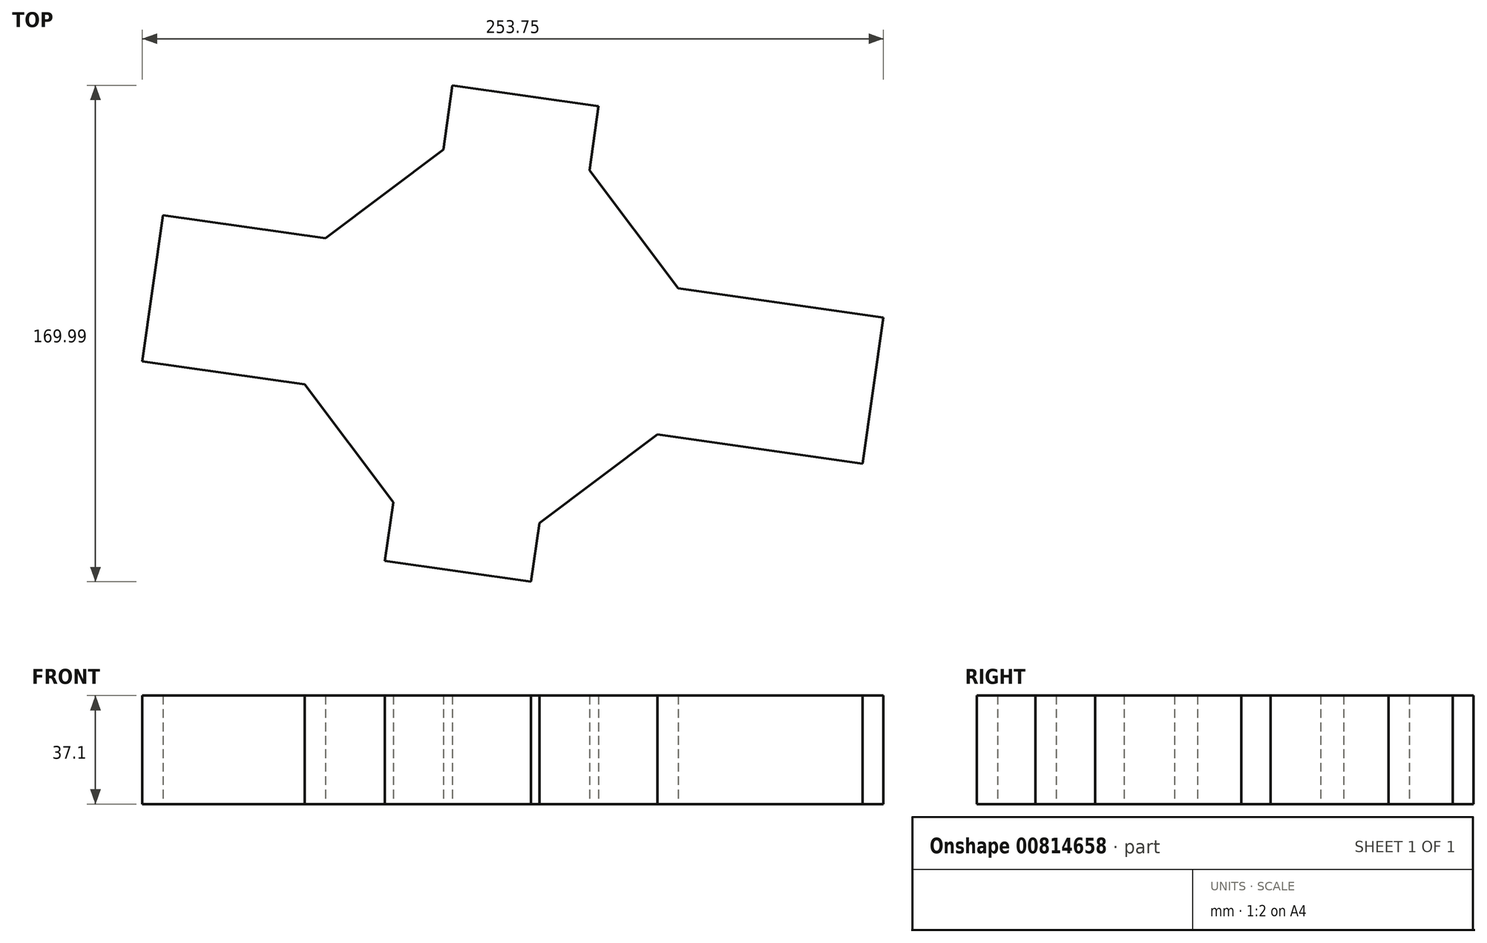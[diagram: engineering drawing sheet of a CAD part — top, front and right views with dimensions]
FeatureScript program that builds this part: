
annotation { "Feature Type Name" : "Feature", "Feature Type Description" : "" }
export const myFeature = defineFeature(function(context is Context, id is Id, definition is map)
    precondition{}
    {
        {
            var Q0;
            Q0=qCreatedBy(makeId("Top.planeOp"),FACE);
            var sketch = newSketch(context, id + "F0", { "sketchPlane" : qUnion([Q0])});
            skCircle(sketch, "E0.cCircle", {"center": v(0, 0) * mm, "radius": 61 * mm, "construction": true});
            skLineSegment(sketch, "E0.0", {"start": v(-63.96, -16.44) * mm, "end": v(-56.85, 33.6) * mm});
            skLineSegment(sketch, "E0.1", {"start": v(-56.85, 33.6) * mm, "end": v(-16.44, 63.96) * mm});
            skLineSegment(sketch, "E0.2", {"start": v(-16.44, 63.96) * mm, "end": v(33.6, 56.85) * mm});
            skLineSegment(sketch, "E0.3", {"start": v(33.6, 56.85) * mm, "end": v(63.96, 16.44) * mm});
            skLineSegment(sketch, "E0.4", {"start": v(63.96, 16.44) * mm, "end": v(56.85, -33.6) * mm});
            skLineSegment(sketch, "E0.5", {"start": v(56.85, -33.6) * mm, "end": v(16.44, -63.96) * mm});
            skLineSegment(sketch, "E0.6", {"start": v(16.44, -63.96) * mm, "end": v(-33.6, -56.85) * mm});
            skLineSegment(sketch, "E0.7", {"start": v(-33.6, -56.85) * mm, "end": v(-63.96, -16.44) * mm});
            skPoint(sketch, "E0.0.midPoint", {"position": v(-60.4, 8.58) * mm});
            skSolve(sketch);
        }
        {
            var Q0;
            Q0=makeQuery(id+"F0.imprint","IMPRINT",FACE,{"disambiguationData":[TD([[makeQuery(id+"F0.imprint","IMPRINT",EDGE,{"derivedFrom":sQuery(id+"F0.wireOp",EDGE,"E0.0")}),-1.0]])]});
            extrude(context, id + "F1", {"entities" : qUnion([Q0]), "depth" : 37.1 * mm, "offsetDistance" : 25 * mm});
        }
        {
            var Q0;
            Q0=makeQuery(id+"F1.opExtrude","SWEPT_FACE",FACE,{"disambiguationData":[OSD([sQuery(id+"F0.wireOp",EDGE,"E0.0")])]});
            extrude(context, id + "F2", {"entities" : qUnion([Q0]), "operationType" : NewBodyOperationType.ADD, "depth" : 56.1 * mm, "offsetDistance" : 25 * mm});
        }
        {
            var Q0;
            Q0=makeQuery(id+"F1.opExtrude","SWEPT_FACE",FACE,{"disambiguationData":[OSD([sQuery(id+"F0.wireOp",EDGE,"E0.4")])]});
            extrude(context, id + "F3", {"entities" : qUnion([Q0]), "operationType" : NewBodyOperationType.ADD, "depth" : 71 * mm, "offsetDistance" : 25 * mm});
        }
        {
            var Q0;
            Q0=makeQuery(id+"F1.opExtrude","SWEPT_FACE",FACE,{"disambiguationData":[OSD([sQuery(id+"F0.wireOp",EDGE,"E0.6")])]});
            extrude(context, id + "F4", {"entities" : qUnion([Q0]), "operationType" : NewBodyOperationType.ADD, "depth" : 20.3 * mm, "offsetDistance" : 25 * mm});
        }
        {
            var Q0;
            Q0=makeQuery(id+"F1.opExtrude","SWEPT_FACE",FACE,{"disambiguationData":[OSD([sQuery(id+"F0.wireOp",EDGE,"E0.2")])]});
            extrude(context, id + "F5", {"entities" : qUnion([Q0]), "operationType" : NewBodyOperationType.ADD, "depth" : 22.2 * mm, "offsetDistance" : 25 * mm});
        }
    });
